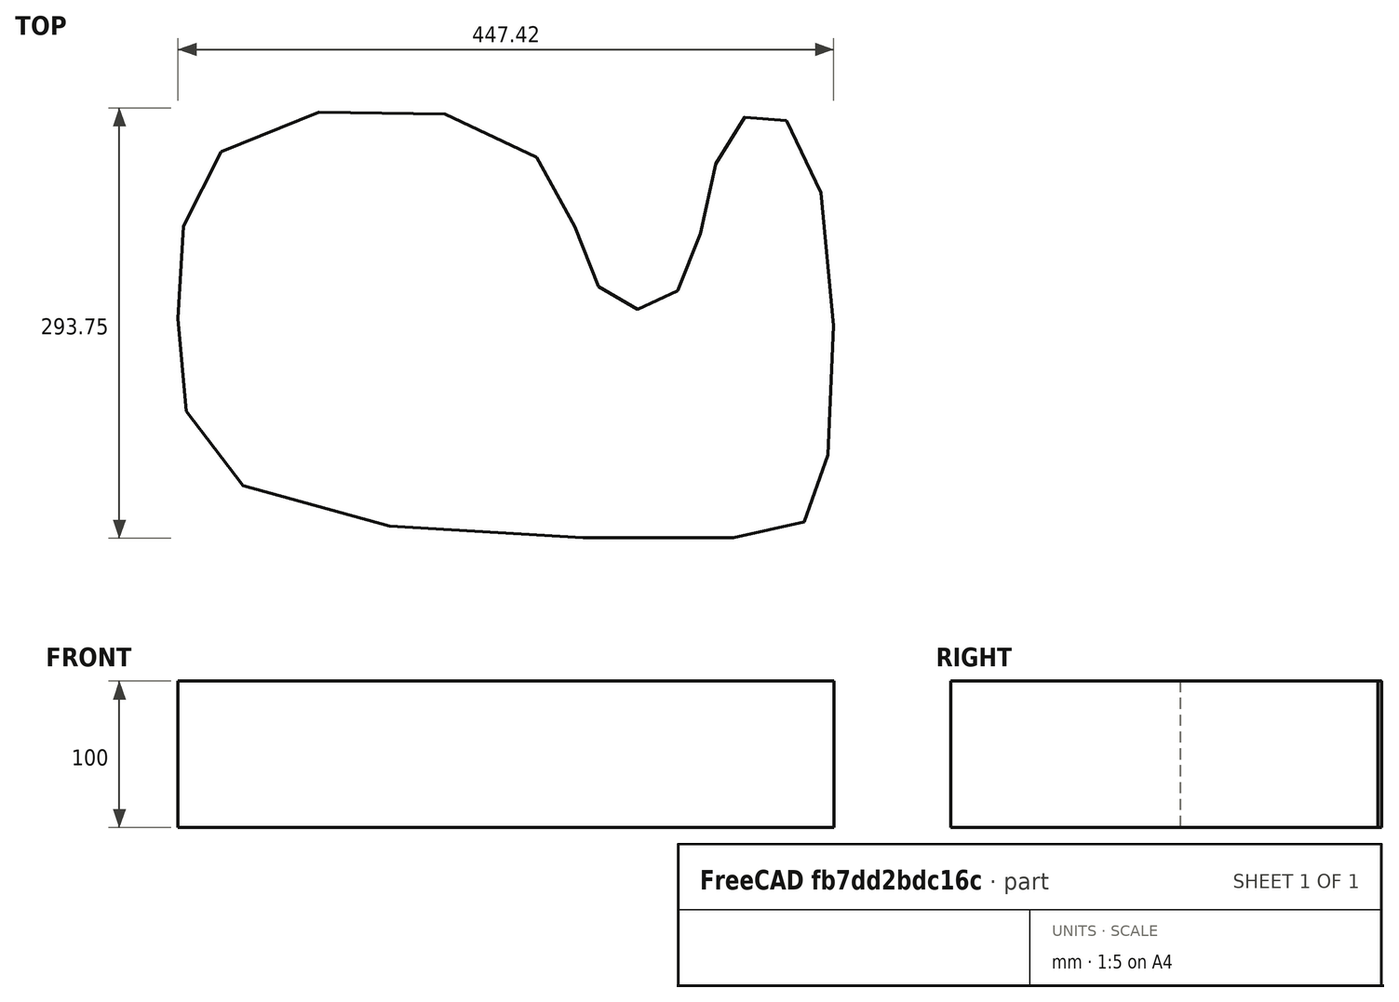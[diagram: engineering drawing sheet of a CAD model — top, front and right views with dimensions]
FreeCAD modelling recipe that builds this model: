
FCSTD DOCUMENT  (FreeCAD 0.18R16093 (Git))
Label: my_contour
License: All rights reserved
LicenseURL: http://en.wikipedia.org/wiki/All_rights_reserved
objects: Sketcher::SketchObject×1, PartDesign::Pad×1, PartDesign::Body×1, Spreadsheet::Sheet×1
note: 4 computed .brp shape members not serialized (recipe doc carries the construction recipe); baked Part::Feature solids carry a one-line shape summary decoded from their .brp

FEATURE [Sketcher::SketchObject] Sketch
  MapMode = 5
  Support = -> [XY_Plane]
  expr: Constraints[44] = cnt.width / 10
  expr: Constraints[43] = cnt.width
  expr: Constraints[45] = cnt.width / 5
  expr: Constraints[46] = cnt.width / 5
  expr: Constraints[35] = cnt.height / 2
  expr: Constraints.H1 = cnt.height / 2
  sketch-geometry (22):
    g0-g9: Circle [constr] x10 (B-spline internal-alignment scaffolding for g10; pole/knot coordinates omitted)
    g10: BSplineCurve PolesCount=10 KnotsCount=11 Degree=3 IsPeriodic=1
    g11-g21: GeomPoint [constr] x11 (B-spline internal-alignment scaffolding for g10; pole/knot coordinates omitted)
  constraints (21):
    c: Equal(g0, g1-g9) x9
    c: InternalAlignment(g0-g9 -> g10) x10
    c: InternalAlignment(g11-g21 -> g10) x11
    c: Vertical(g0,g1)
    c: Vertical(g1,g2)
    c: Vertical(g8,g7)
    c: Horizontal(g5,g4)
    c: DistanceY(g1,g2) = 150  'H1'
    c: DistanceY(g0,g1) = 150
    c: Horizontal(g1,g4)
    c: Horizontal(g2,g3)
    c: Horizontal(g3,g6)
    c: Horizontal(g6,g7)
    c: Horizontal(g0,g9)
    c: Horizontal(g9,g8)
    c: Vertical(g5,g6)
    c: DistanceX(g0,g8) = 450
    c: DistanceX(g9,g8) = 45
    c: DistanceX(g6,g7) = 90
    c: DistanceX(g3,g6) = 90
    c: Vertical(g4,g3)
FEATURE [PartDesign::Pad] Pad
  Length = 100
  Length2 = 100
  Profile = -> Sketch
  Type = 0
  expr: Length = cnt.D
FEATURE [PartDesign::Body] Body
  Group = -> [Sketch,Pad]
  Origin = -> Origin
  Tip = -> Pad
FEATURE [Spreadsheet::Sheet] Spreadsheet  label="cnt"
  cells = A1=Contourparameters; A2=Breedte; B2(width)=450; A3=Diepte; B3(height)=300; A4=Hoogte; B4(D)=100
